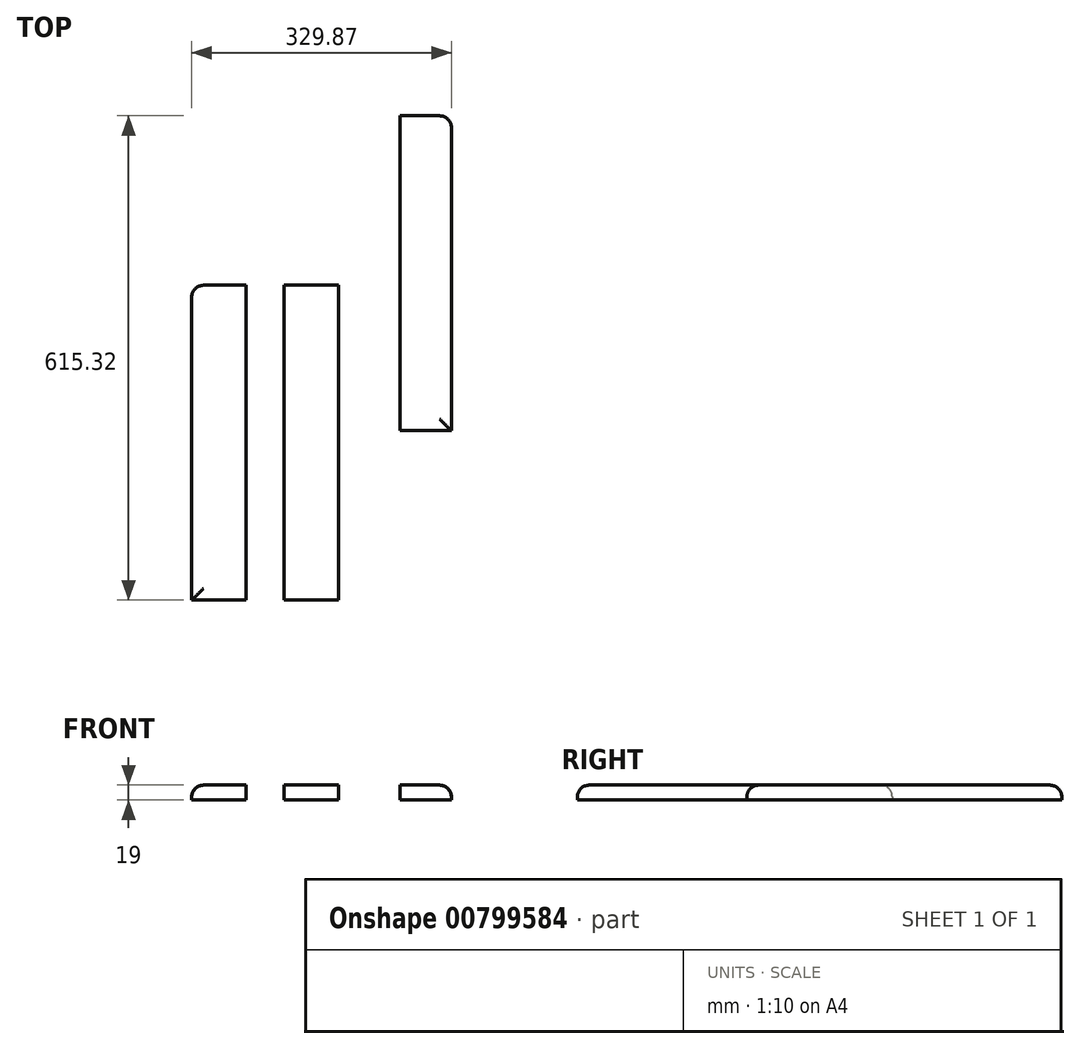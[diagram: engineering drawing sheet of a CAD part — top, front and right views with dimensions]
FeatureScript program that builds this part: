
annotation { "Feature Type Name" : "Feature", "Feature Type Description" : "" }
export const myFeature = defineFeature(function(context is Context, id is Id, definition is map)
    precondition{}
    {
        {
            var Q0;
            Q0=qCreatedBy(makeId("Top.planeOp"),FACE);
            var sketch = newSketch(context, id + "F0", { "sketchPlane" : qUnion([Q0])});
            skLineSegment(sketch, "E0.bottom", {"start": v(-854.9, 400) * mm, "end": v(-785.9, 400) * mm});
            skLineSegment(sketch, "E0.top", {"start": v(-854.9, 0) * mm, "end": v(-785.9, 0) * mm});
            skLineSegment(sketch, "E0.left", {"start": v(-854.9, 400) * mm, "end": v(-854.9, 0) * mm});
            skLineSegment(sketch, "E0.right", {"start": v(-785.9, 400) * mm, "end": v(-785.9, 0) * mm});
            skSolve(sketch);
        }
        {
            var Q0;
            Q0=qCreatedBy(makeId("Top.planeOp"),FACE);
            var sketch = newSketch(context, id + "F1", { "sketchPlane" : qUnion([Q0])});
            skLineSegment(sketch, "E1.bottom", {"start": v(-737.36, 400) * mm, "end": v(-668.36, 400) * mm});
            skLineSegment(sketch, "E1.top", {"start": v(-737.36, 0) * mm, "end": v(-668.36, 0) * mm});
            skLineSegment(sketch, "E1.left", {"start": v(-737.36, 400) * mm, "end": v(-737.36, 0) * mm});
            skLineSegment(sketch, "E1.right", {"start": v(-668.36, 400) * mm, "end": v(-668.36, 0) * mm});
            skSolve(sketch);
        }
        {
            var Q0;
            Q0=qCreatedBy(makeId("Top.planeOp"),FACE);
            var sketch = newSketch(context, id + "F2", { "sketchPlane" : qUnion([Q0])});
            skLineSegment(sketch, "E2.bottom", {"start": v(-590.04, 615.32) * mm, "end": v(-525.04, 615.32) * mm});
            skLineSegment(sketch, "E2.top", {"start": v(-590.04, 215.32) * mm, "end": v(-525.04, 215.32) * mm});
            skLineSegment(sketch, "E2.left", {"start": v(-590.04, 615.32) * mm, "end": v(-590.04, 215.32) * mm});
            skLineSegment(sketch, "E2.right", {"start": v(-525.04, 615.32) * mm, "end": v(-525.04, 215.32) * mm});
            skSolve(sketch);
        }
        {
            var Q0;
            Q0=makeQuery(id+"F0.imprint","IMPRINT",FACE,{"disambiguationData":[TD([[makeQuery(id+"F0.imprint","IMPRINT",EDGE,{"derivedFrom":sQuery(id+"F0.wireOp",EDGE,"E0.bottom")}),-1.0]])]});
            extrude(context, id + "F3", {"entities" : qUnion([Q0]), "depth" : 19 * mm, "offsetDistance" : 25 * mm});
        }
        {
            var Q0;
            Q0=makeQuery(id+"F1.imprint","IMPRINT",FACE,{"disambiguationData":[TD([[makeQuery(id+"F1.imprint","IMPRINT",EDGE,{"derivedFrom":sQuery(id+"F1.wireOp",EDGE,"E1.bottom")}),-1.0]])]});
            extrude(context, id + "F4", {"entities" : qUnion([Q0]), "depth" : 19 * mm, "offsetDistance" : 25 * mm});
        }
        {
            var Q0;
            Q0=makeQuery(id+"F2.imprint","IMPRINT",FACE,{"disambiguationData":[TD([[makeQuery(id+"F2.imprint","IMPRINT",EDGE,{"derivedFrom":sQuery(id+"F2.wireOp",EDGE,"E2.bottom")}),-1.0]])]});
            extrude(context, id + "F5", {"entities" : qUnion([Q0]), "depth" : 19 * mm, "offsetDistance" : 25 * mm});
        }
        {
            var Q0;
            Q0=makeQuery(id+"F3.opExtrude","CAP_EDGE",EDGE,{"disambiguationData":[OSD([sQuery(id+"F0.wireOp",EDGE,"E0.left")])],"isStart":false});
            var Q1;
            Q1=makeQuery(id+"F3.opExtrude","CAP_EDGE",EDGE,{"disambiguationData":[OSD([sQuery(id+"F0.wireOp",EDGE,"E0.top")])],"isStart":false});
            fillet(context, id + "F6", {"entities" : qUnion([Q0, Q1]), "radius" : 15 * mm, "tangentPropagation" : true, "allowEdgeOverflow" : false});
        }
        {
            var Q0;
            Q0=makeQuery(id+"F4.opExtrude","CAP_EDGE",EDGE,{"disambiguationData":[OSD([sQuery(id+"F1.wireOp",EDGE,"E1.top")])],"isStart":false});
            var Q1;
            Q1=makeQuery(id+"F4.opExtrude","CAP_EDGE",EDGE,{"disambiguationData":[OSD([sQuery(id+"F1.wireOp",EDGE,"E1.bottom")])],"isStart":false});
            fillet(context, id + "F7", {"entities" : qUnion([Q0, Q1]), "radius" : 15 * mm, "tangentPropagation" : true, "allowEdgeOverflow" : false});
        }
        {
            var Q0;
            Q0=makeQuery(id+"F5.opExtrude","CAP_EDGE",EDGE,{"disambiguationData":[OSD([sQuery(id+"F2.wireOp",EDGE,"E2.right")])],"isStart":false});
            var Q1;
            Q1=makeQuery(id+"F5.opExtrude","CAP_EDGE",EDGE,{"disambiguationData":[OSD([sQuery(id+"F2.wireOp",EDGE,"E2.top")])],"isStart":false});
            fillet(context, id + "F8", {"entities" : qUnion([Q0, Q1]), "radius" : 15 * mm, "tangentPropagation" : true, "allowEdgeOverflow" : false});
        }
        {
            var Q0;
            Q0=makeQuery(id+"F5.opExtrude","CAP_EDGE",EDGE,{"disambiguationData":[OSD([sQuery(id+"F2.wireOp",EDGE,"E2.bottom")])],"isStart":false});
            fillet(context, id + "F9", {"entities" : qUnion([Q0]), "radius" : 15 * mm, "tangentPropagation" : true, "allowEdgeOverflow" : false});
        }
        {
            var Q0;
            Q0=makeQuery(id+"F3.opExtrude","CAP_EDGE",EDGE,{"disambiguationData":[OSD([sQuery(id+"F0.wireOp",EDGE,"E0.bottom")])],"isStart":false});
            fillet(context, id + "F10", {"entities" : qUnion([Q0]), "radius" : 15 * mm, "tangentPropagation" : true, "allowEdgeOverflow" : false});
        }
    });
